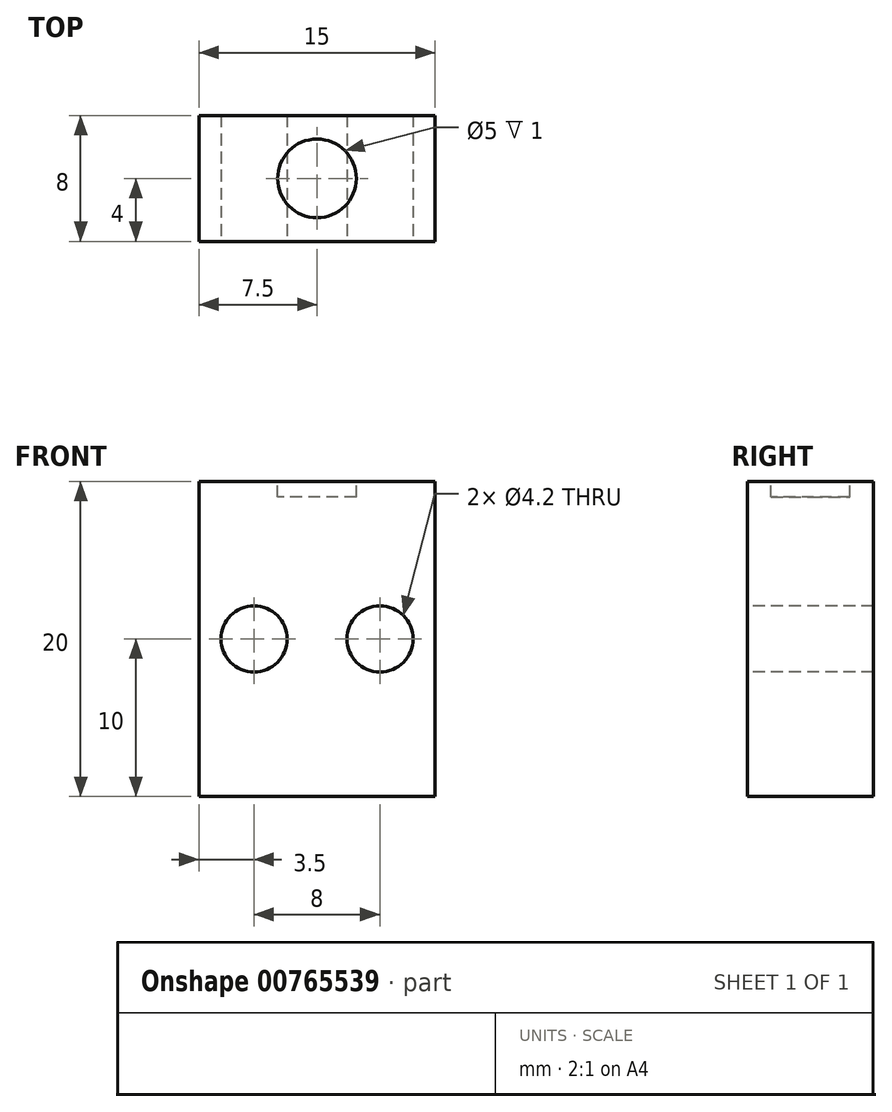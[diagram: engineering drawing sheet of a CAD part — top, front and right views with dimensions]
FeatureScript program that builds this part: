
annotation { "Feature Type Name" : "Feature", "Feature Type Description" : "" }
export const myFeature = defineFeature(function(context is Context, id is Id, definition is map)
    precondition{}
    {
        {
            var Q0;
            Q0=qCreatedBy(makeId("Top.planeOp"),FACE);
            var sketch = newSketch(context, id + "F0", { "sketchPlane" : qUnion([Q0])});
            skLineSegment(sketch, "E0.bottom", {"start": v(0, 0) * mm, "end": v(15, 0) * mm});
            skLineSegment(sketch, "E0.top", {"start": v(0, 8) * mm, "end": v(15, 8) * mm});
            skLineSegment(sketch, "E0.left", {"start": v(0, 0) * mm, "end": v(0, 8) * mm});
            skLineSegment(sketch, "E0.right", {"start": v(15, 0) * mm, "end": v(15, 8) * mm});
            skSolve(sketch);
        }
        {
            var Q0;
            Q0 = qSketchRegion(id + "F0", true);
            extrude(context, id + "F1", {"entities" : qUnion([Q0]), "depth" : 20 * mm, "offsetDistance" : 25 * mm});
        }
        {
            var Q0;
            Q0=makeQuery(id+"F1.opExtrude","SWEPT_FACE",FACE,{"disambiguationData":[OSD([sQuery(id+"F0.wireOp",EDGE,"E0.bottom")])]});
            var sketch = newSketch(context, id + "F2", { "sketchPlane" : qUnion([Q0])});
            skCircle(sketch, "E1", {"center": v(3.5, 10) * mm, "radius": 2.1 * mm});
            skPoint(sketch, "E1.centerSnap0", {"position": v(15, 10) * mm});
            skCircle(sketch, "E2", {"center": v(11.5, 10) * mm, "radius": 2.1 * mm});
            skSolve(sketch);
        }
        {
            var Q0;
            Q0 = qSketchRegion(id + "F2", true);
            extrude(context, id + "F3", {"entities" : qUnion([Q0]), "operationType" : NewBodyOperationType.REMOVE, "oppositeDirection" : true, "depth" : 25 * mm, "offsetDistance" : 25 * mm});
        }
        {
            var Q0;
            Q0=makeQuery(id+"F1.opExtrude","CAP_FACE",FACE,{"disambiguationData":[OSD([sQuery(id+"F0.wireOp",EDGE,"E0.bottom"),sQuery(id+"F0.wireOp",EDGE,"E0.top"),sQuery(id+"F0.wireOp",EDGE,"E0.left"),sQuery(id+"F0.wireOp",EDGE,"E0.right")])],"isStart":false});
            var sketch = newSketch(context, id + "F4", { "sketchPlane" : qUnion([Q0])});
            skCircle(sketch, "E3", {"center": v(7.5, 4) * mm, "radius": 2.5 * mm});
            skSolve(sketch);
        }
        {
            var Q0;
            Q0 = qSketchRegion(id + "F4", true);
            extrude(context, id + "F5", {"entities" : qUnion([Q0]), "operationType" : NewBodyOperationType.REMOVE, "oppositeDirection" : true, "depth" : 1 * mm, "offsetDistance" : 25 * mm});
        }
    });
